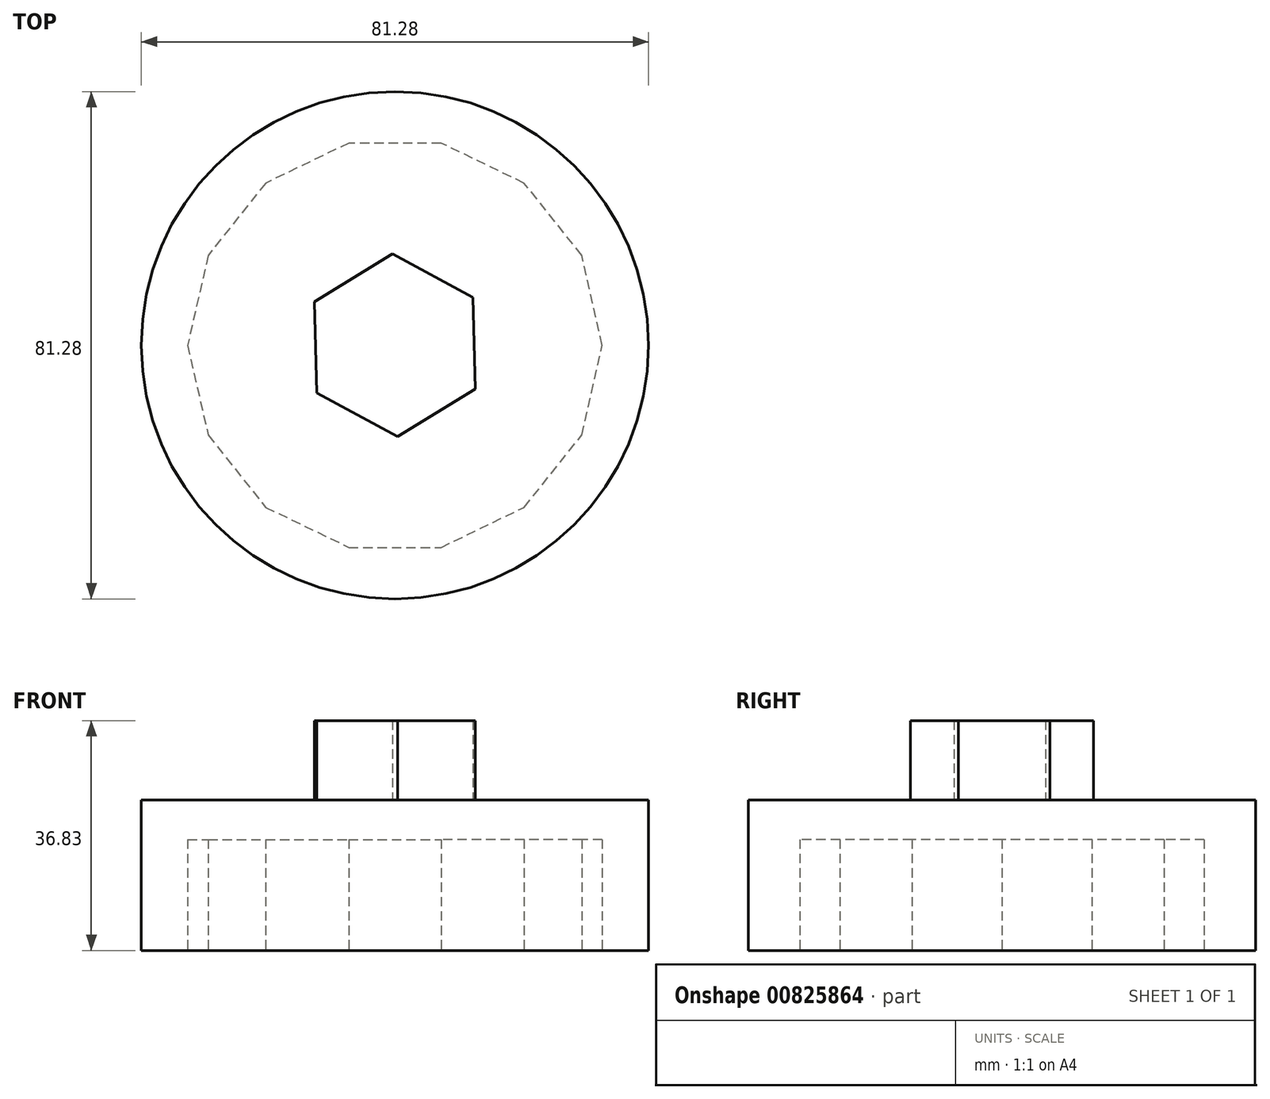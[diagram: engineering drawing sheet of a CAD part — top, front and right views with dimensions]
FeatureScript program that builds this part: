
annotation { "Feature Type Name" : "Feature", "Feature Type Description" : "" }
export const myFeature = defineFeature(function(context is Context, id is Id, definition is map)
    precondition{}
    {
        {
            var Q0;
            Q0=qCreatedBy(makeId("Top.planeOp"),FACE);
            var sketch = newSketch(context, id + "F0", { "sketchPlane" : qUnion([Q0])});
            skLineSegment(sketch, "E0.0", {"start": v(-7.4, -32.39) * mm, "end": v(7.4, -32.39) * mm});
            skLineSegment(sketch, "E1.1.0", {"start": v(7.4, -32.38) * mm, "end": v(20.71, -25.97) * mm});
            skLineSegment(sketch, "E1.2.0", {"start": v(20.71, -25.97) * mm, "end": v(29.93, -14.41) * mm});
            skPoint(sketch, "E1.center", {"position": v(0, 0) * mm});
            skLineSegment(sketch, "E2.1.3.0", {"start": v(29.93, -14.41) * mm, "end": v(33.22, 0) * mm});
            skLineSegment(sketch, "E2.1.4.0", {"start": v(33.22, 0) * mm, "end": v(29.93, 14.41) * mm});
            skLineSegment(sketch, "E2.1.5.0", {"start": v(29.93, 14.41) * mm, "end": v(20.71, 25.97) * mm});
            skLineSegment(sketch, "E2.1.6.0", {"start": v(20.71, 25.97) * mm, "end": v(7.4, 32.38) * mm});
            skLineSegment(sketch, "E2.1.7.0", {"start": v(7.4, 32.38) * mm, "end": v(-7.4, 32.39) * mm});
            skLineSegment(sketch, "E2.1.8.0", {"start": v(-7.4, 32.39) * mm, "end": v(-20.71, 25.97) * mm});
            skLineSegment(sketch, "E2.1.9.0", {"start": v(-20.71, 25.97) * mm, "end": v(-29.93, 14.41) * mm});
            skLineSegment(sketch, "E2.1.10.0", {"start": v(-29.93, 14.41) * mm, "end": v(-33.22, 0) * mm});
            skLineSegment(sketch, "E2.1.11.0", {"start": v(-33.22, 0) * mm, "end": v(-29.93, -14.41) * mm});
            skLineSegment(sketch, "E2.1.12.0", {"start": v(-29.93, -14.41) * mm, "end": v(-20.71, -25.97) * mm});
            skLineSegment(sketch, "E2.1.13.0", {"start": v(-20.71, -25.97) * mm, "end": v(-7.4, -32.39) * mm});
            skPoint(sketch, "E3.orphan", {"position": v(-31.57, 7.2) * mm});
            skPoint(sketch, "E4.orphan", {"position": v(-25.32, 20.2) * mm});
            skPoint(sketch, "E5.orphan", {"position": v(-14.05, 29.18) * mm});
            skPoint(sketch, "E6.orphan", {"position": v(0, 32.39) * mm});
            skPoint(sketch, "E7.orphan", {"position": v(14.05, 29.18) * mm});
            skPoint(sketch, "E8.orphan", {"position": v(25.32, 20.2) * mm});
            skPoint(sketch, "E9.orphan", {"position": v(31.57, 7.2) * mm});
            skPoint(sketch, "E10.orphan", {"position": v(31.57, -7.2) * mm});
            skPoint(sketch, "E11.orphan", {"position": v(25.32, -20.2) * mm});
            skPoint(sketch, "E12.orphan", {"position": v(14.05, -29.18) * mm});
            skPoint(sketch, "E13.orphan", {"position": v(0, -32.39) * mm});
            skPoint(sketch, "E14.orphan", {"position": v(-14.05, -29.18) * mm});
            skPoint(sketch, "E15.orphan", {"position": v(-25.32, -20.2) * mm});
            skPoint(sketch, "E16.orphan", {"position": v(-31.57, -7.2) * mm});
            skPoint(sketch, "E17.orphan", {"position": v(-57.34, -19.96) * mm});
            skPoint(sketch, "E18.orphan", {"position": v(-60.33, 6.9) * mm});
            skPoint(sketch, "E19.orphan", {"position": v(-51.36, 32.39) * mm});
            skPoint(sketch, "E20.orphan", {"position": v(-32.22, 51.46) * mm});
            skPoint(sketch, "E21.orphan", {"position": v(-6.7, 60.35) * mm});
            skPoint(sketch, "E22.orphan", {"position": v(20.14, 57.28) * mm});
            skPoint(sketch, "E23.orphan", {"position": v(43, 42.87) * mm});
            skPoint(sketch, "E24.orphan", {"position": v(57.34, 19.96) * mm});
            skPoint(sketch, "E25.orphan", {"position": v(60.33, -6.9) * mm});
            skPoint(sketch, "E26.orphan", {"position": v(51.36, -32.39) * mm});
            skPoint(sketch, "E27.orphan", {"position": v(32.22, -51.46) * mm});
            skPoint(sketch, "E28.orphan", {"position": v(6.7, -60.35) * mm});
            skPoint(sketch, "E29.orphan", {"position": v(-20.14, -57.28) * mm});
            skPoint(sketch, "E30.orphan", {"position": v(-43, -42.87) * mm});
            skCircle(sketch, "E31", {"center": v(0, 0) * mm, "radius": 40.64 * mm});
            skSolve(sketch);
        }
        {
            var Q0;
            Q0=makeQuery(id+"F0.imprint","IMPRINT",FACE,{"disambiguationData":[TD([[makeQuery(id+"F0.imprint","IMPRINT",EDGE,{"derivedFrom":sQuery(id+"F0.wireOp",EDGE,"E0.0")}),-1.0]])]});
            extrude(context, id + "F1", {"entities" : qUnion([Q0]), "depth" : 17.78 * mm, "offsetDistance" : 25.4 * mm});
        }
        {
            var Q0;
            Q0=makeQuery(id+"F1.opExtrude","CAP_FACE",FACE,{"disambiguationData":[OSD([sQuery(id+"F0.wireOp",EDGE,"E0.0"),sQuery(id+"F0.wireOp",EDGE,"E1.1.0"),sQuery(id+"F0.wireOp",EDGE,"E1.2.0"),sQuery(id+"F0.wireOp",EDGE,"E2.1.3.0"),sQuery(id+"F0.wireOp",EDGE,"E2.1.4.0"),sQuery(id+"F0.wireOp",EDGE,"E2.1.5.0"),sQuery(id+"F0.wireOp",EDGE,"E2.1.6.0"),sQuery(id+"F0.wireOp",EDGE,"E2.1.7.0"),sQuery(id+"F0.wireOp",EDGE,"E2.1.8.0"),sQuery(id+"F0.wireOp",EDGE,"E2.1.9.0"),sQuery(id+"F0.wireOp",EDGE,"E2.1.10.0"),sQuery(id+"F0.wireOp",EDGE,"E2.1.11.0"),sQuery(id+"F0.wireOp",EDGE,"E2.1.12.0"),sQuery(id+"F0.wireOp",EDGE,"E2.1.13.0"),sQuery(id+"F0.wireOp",EDGE,"E31")])],"isStart":false});
            var sketch = newSketch(context, id + "F2", { "sketchPlane" : qUnion([Q0])});
            skCircle(sketch, "E32", {"center": v(0, 0) * mm, "radius": 40.64 * mm});
            skSolve(sketch);
        }
        {
            var Q0;
            Q0 = qSketchRegion(id + "F2", true);
            extrude(context, id + "F3", {"entities" : qUnion([Q0]), "operationType" : NewBodyOperationType.ADD, "depth" : 6.35 * mm, "offsetDistance" : 25.4 * mm});
        }
        {
            var Q0;
            Q0=makeQuery(id+"F3.opExtrude","CAP_FACE",FACE,{"disambiguationData":[OSD([sQuery(id+"F2.wireOp",EDGE,"E32")])],"isStart":false});
            var sketch = newSketch(context, id + "F4", { "sketchPlane" : qUnion([Q0])});
            skCircle(sketch, "E33.cCircle", {"center": v(0, 0) * mm, "radius": 12.7 * mm, "construction": true});
            skLineSegment(sketch, "E33.0", {"start": v(-0.4, 14.66) * mm, "end": v(12.5, 7.67) * mm});
            skLineSegment(sketch, "E33.1", {"start": v(12.5, 7.67) * mm, "end": v(12.9, -6.99) * mm});
            skLineSegment(sketch, "E33.2", {"start": v(12.9, -6.99) * mm, "end": v(0.4, -14.66) * mm});
            skLineSegment(sketch, "E33.3", {"start": v(0.4, -14.66) * mm, "end": v(-12.5, -7.67) * mm});
            skLineSegment(sketch, "E33.4", {"start": v(-12.5, -7.67) * mm, "end": v(-12.9, 6.99) * mm});
            skLineSegment(sketch, "E33.5", {"start": v(-12.9, 6.99) * mm, "end": v(-0.4, 14.66) * mm});
            skPoint(sketch, "E33.0.midPoint", {"position": v(6.05, 11.17) * mm});
            skSolve(sketch);
        }
        {
            var Q0;
            Q0 = qSketchRegion(id + "F4", true);
            extrude(context, id + "F5", {"entities" : qUnion([Q0]), "operationType" : NewBodyOperationType.ADD, "depth" : 12.7 * mm, "offsetDistance" : 25.4 * mm});
        }
    });
